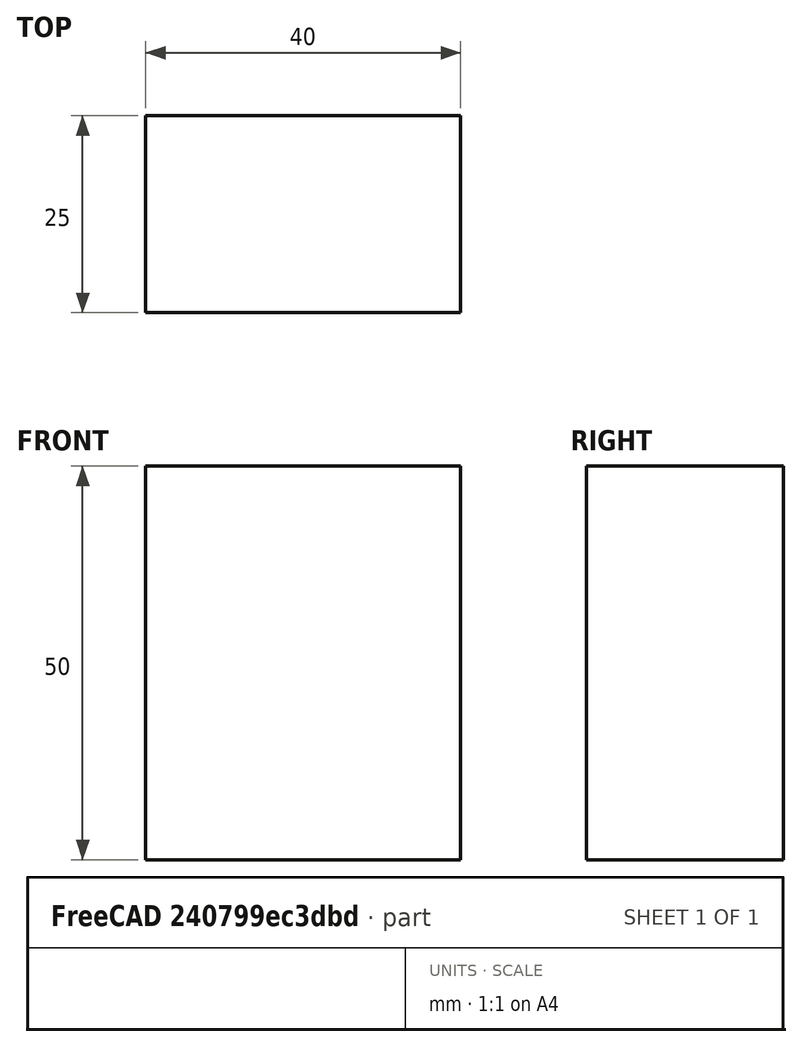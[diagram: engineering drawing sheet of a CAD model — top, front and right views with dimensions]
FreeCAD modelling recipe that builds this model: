
FCSTD DOCUMENT  (FreeCAD 0.15R4671 (Git))
Label: Flat Bar 40x25 EN10058 S235JR
License: All rights reserved
LicenseURL: http://en.wikipedia.org/wiki/All_rights_reserved
objects: Sketcher::SketchObject×1, Part::Extrusion×1
note: 2 computed .brp shape members not serialized (recipe doc carries the construction recipe); baked Part::Feature solids carry a one-line shape summary decoded from their .brp

FEATURE [Sketcher::SketchObject] Sketch
  sketch-geometry (4):
    g0: LineSegment StartX=-20 StartY=-12.5 StartZ=0 EndX=20 EndY=-12.5 EndZ=0
    g1: LineSegment StartX=20 StartY=-12.5 StartZ=0 EndX=20 EndY=12.5 EndZ=0
    g2: LineSegment StartX=20 StartY=12.5 StartZ=0 EndX=-20 EndY=12.5 EndZ=0
    g3: LineSegment StartX=-20 StartY=12.5 StartZ=0 EndX=-20 EndY=-12.5 EndZ=0
  constraints (12):
    c: Coincident(g0,g1)
    c: Coincident(g1,g2)
    c: Coincident(g2,g3)
    c: Coincident(g3,g0)
    c: Horizontal(g0)
    c: Horizontal(g2)
    c: Vertical(g1)
    c: Vertical(g3)
    c: Symmetric(g1,g2,g-2)
    c: Symmetric(g0,g1,g-1)
    c: DistanceY(g1) = 25
    c: DistanceX(g0) = 40
FEATURE [Part::Extrusion] Extrude  label="Flat Bar 40x25 EN10058 S235JR"
  Base = -> Sketch
  Dir = (0,0,50)
  Solid = true
